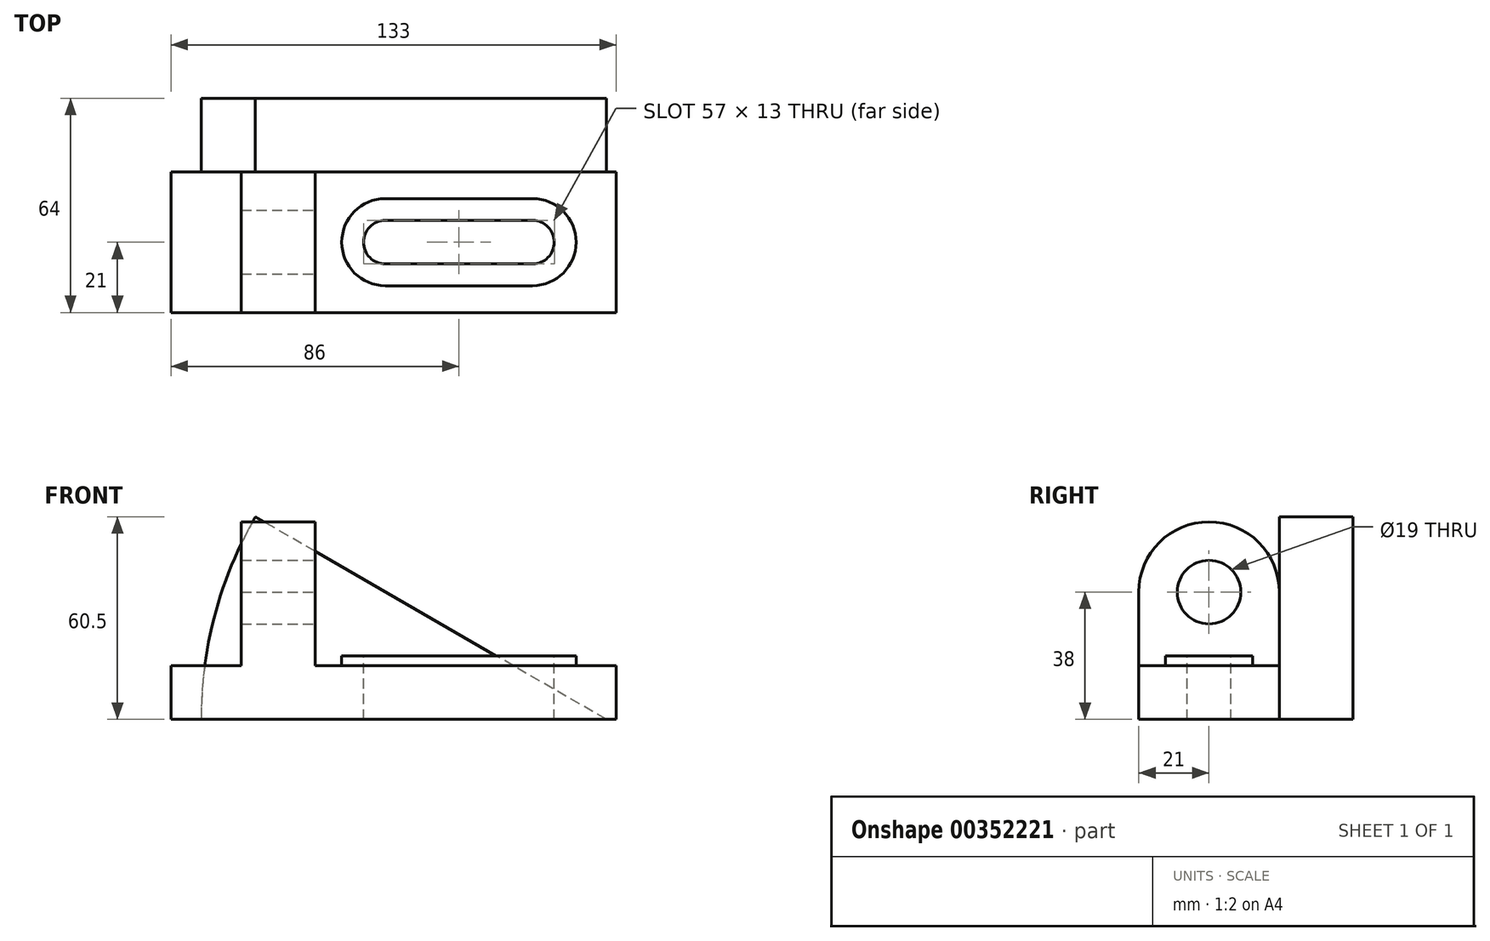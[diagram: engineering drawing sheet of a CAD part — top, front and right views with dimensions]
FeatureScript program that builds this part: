
annotation { "Feature Type Name" : "Feature", "Feature Type Description" : "" }
export const myFeature = defineFeature(function(context is Context, id is Id, definition is map)
    precondition{}
    {
        {
            var Q0;
            Q0=qCreatedBy(makeId("Front.planeOp"),FACE);
            var sketch = newSketch(context, id + "F0", { "sketchPlane" : qUnion([Q0])});
            skLineSegment(sketch, "E0", {"start": v(0, 0) * mm, "end": v(0, 16) * mm});
            skLineSegment(sketch, "E1", {"start": v(0, 16) * mm, "end": v(21, 16) * mm});
            skLineSegment(sketch, "E2", {"start": v(21, 16) * mm, "end": v(21, 86) * mm});
            skLineSegment(sketch, "E3", {"start": v(21, 86) * mm, "end": v(43, 86) * mm});
            skLineSegment(sketch, "E4", {"start": v(43, 86) * mm, "end": v(43, 16) * mm});
            skLineSegment(sketch, "E5", {"start": v(43, 16) * mm, "end": v(133, 16) * mm});
            skLineSegment(sketch, "E6", {"start": v(133, 16) * mm, "end": v(133, 0) * mm});
            skLineSegment(sketch, "E7", {"start": v(133, 0) * mm, "end": v(0, 0) * mm});
            skSolve(sketch);
        }
        {
            var Q0;
            Q0 = qSketchRegion(id + "F0", true);
            extrude(context, id + "F1", {"entities" : qUnion([Q0]), "depth" : 42 * mm});
        }
        {
            var Q0;
            Q0=makeQuery(id+"F1.opExtrude","SWEPT_FACE",FACE,{"disambiguationData":[OSD([sQuery(id+"F0.wireOp",EDGE,"E4")])]});
            var sketch = newSketch(context, id + "F2", { "sketchPlane" : qUnion([Q0])});
            skCircle(sketch, "E8", {"center": v(-21, 38) * mm, "radius": 9.5 * mm});
            skPoint(sketch, "E8.centerSnap0", {"position": v(-21, 16) * mm});
            skArc(sketch, "E9", {"start": v(-42, 38) * mm, "mid": v(-21, 59) * mm, "end": v(0, 38) * mm});
            skLineSegment(sketch, "E10", {"start": v(-42, 38) * mm, "end": v(-42, 86) * mm});
            skLineSegment(sketch, "E11", {"start": v(-42, 86) * mm, "end": v(0, 86) * mm});
            skLineSegment(sketch, "E12", {"start": v(0, 86) * mm, "end": v(0, 38) * mm});
            skSolve(sketch);
        }
        {
            var Q0;
            Q0 = qSketchRegion(id + "F2", true);
            extrude(context, id + "F3", {"entities" : qUnion([Q0]), "operationType" : NewBodyOperationType.REMOVE, "endBound" : BoundingType.THROUGH_ALL, "oppositeDirection" : true, "depth" : 25 * mm});
        }
        {
            var Q0;
            Q0=makeQuery(id+"F1.opExtrude","SWEPT_FACE",FACE,{"disambiguationData":[OSD([sQuery(id+"F0.wireOp",EDGE,"E5")])]});
            var sketch = newSketch(context, id + "F4", { "sketchPlane" : qUnion([Q0])});
            skLineSegment(sketch, "E13", {"start": v(64, -8) * mm, "end": v(108, -8) * mm});
            skLineSegment(sketch, "E14", {"start": v(64, -34) * mm, "end": v(108, -34) * mm});
            skArc(sketch, "E15", {"start": v(64, -8) * mm, "mid": v(51, -21) * mm, "end": v(64, -34) * mm});
            skArc(sketch, "E16", {"start": v(108, -8) * mm, "mid": v(121, -21) * mm, "end": v(108, -34) * mm});
            skLineSegment(sketch, "E17", {"start": v(133, -21) * mm, "end": v(157.52, -21) * mm, "construction": true});
            skPoint(sketch, "E17.endSnap0", {"position": v(133, -21) * mm});
            skSolve(sketch);
        }
        {
            var Q0;
            Q0 = qSketchRegion(id + "F4", true);
            extrude(context, id + "F5", {"entities" : qUnion([Q0]), "operationType" : NewBodyOperationType.ADD, "depth" : 3 * mm});
        }
        {
            var Q0;
            Q0=makeQuery(id+"F5.opExtrude","CAP_FACE",FACE,{"disambiguationData":[OSD([sQuery(id+"F4.wireOp",EDGE,"E13"),sQuery(id+"F4.wireOp",EDGE,"E14"),sQuery(id+"F4.wireOp",EDGE,"E15"),sQuery(id+"F4.wireOp",EDGE,"E16")])],"isStart":false});
            var sketch = newSketch(context, id + "F6", { "sketchPlane" : qUnion([Q0])});
            skLineSegment(sketch, "E18", {"start": v(64, -14.5) * mm, "end": v(108, -14.5) * mm});
            skLineSegment(sketch, "E19", {"start": v(64, -27.5) * mm, "end": v(108, -27.5) * mm});
            skArc(sketch, "E20", {"start": v(64, -14.5) * mm, "mid": v(57.5, -21) * mm, "end": v(64, -27.5) * mm});
            skArc(sketch, "E21", {"start": v(108, -14.5) * mm, "mid": v(114.5, -21) * mm, "end": v(108, -27.5) * mm});
            skSolve(sketch);
        }
        {
            var Q0;
            Q0 = qSketchRegion(id + "F6", true);
            extrude(context, id + "F7", {"entities" : qUnion([Q0]), "operationType" : NewBodyOperationType.REMOVE, "endBound" : BoundingType.THROUGH_ALL, "oppositeDirection" : true, "depth" : 25 * mm});
        }
        {
            var Q0;
            Q0=makeQuery(id+"F1.opExtrude","CAP_FACE",FACE,{"disambiguationData":[OSD([sQuery(id+"F0.wireOp",EDGE,"E0"),sQuery(id+"F0.wireOp",EDGE,"E1"),sQuery(id+"F0.wireOp",EDGE,"E2"),sQuery(id+"F0.wireOp",EDGE,"E3"),sQuery(id+"F0.wireOp",EDGE,"E4"),sQuery(id+"F0.wireOp",EDGE,"E5"),sQuery(id+"F0.wireOp",EDGE,"E6"),sQuery(id+"F0.wireOp",EDGE,"E7")])],"isStart":true});
            var sketch = newSketch(context, id + "F8", { "sketchPlane" : qUnion([Q0])});
            skLineSegment(sketch, "E22", {"start": v(-133, 0) * mm, "end": v(-130, 0) * mm});
            skLineSegment(sketch, "E23", {"start": v(-130, 0) * mm, "end": v(-25.21, 60.5) * mm});
            skLineSegment(sketch, "E24", {"start": v(-130, 0) * mm, "end": v(-9, 0) * mm});
            skArc(sketch, "E25", {"start": v(-9, 0) * mm, "mid": v(-13.12, 31.32) * mm, "end": v(-25.21, 60.5) * mm});
            skSolve(sketch);
        }
        {
            var Q0;
            Q0 = qSketchRegion(id + "F8", true);
            extrude(context, id + "F9", {"entities" : qUnion([Q0]), "operationType" : NewBodyOperationType.ADD, "depth" : 22 * mm});
        }
    });
